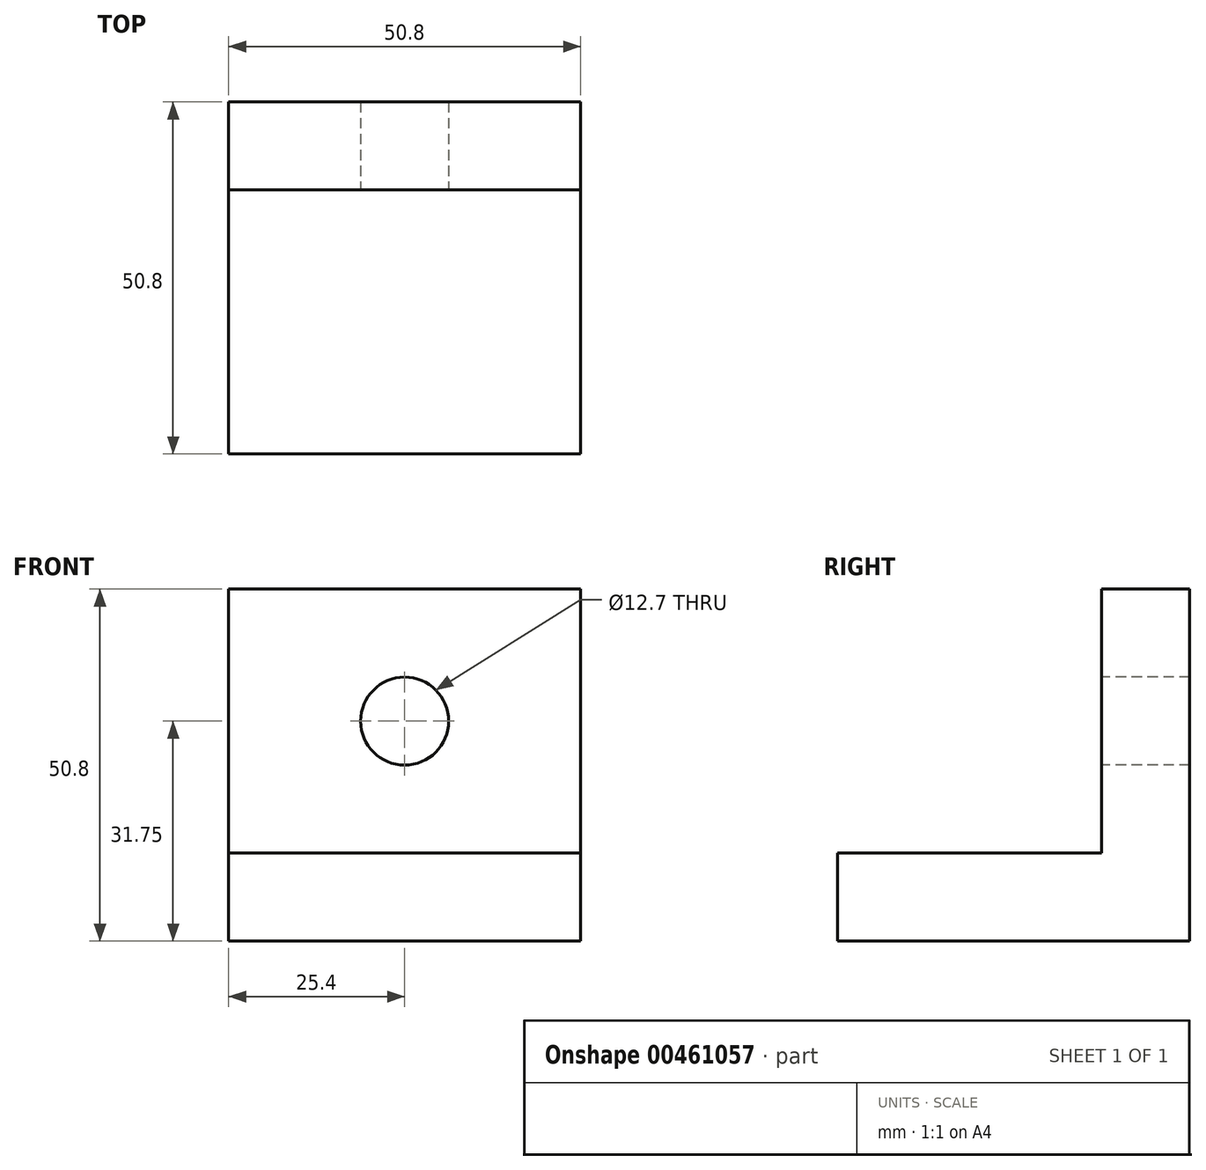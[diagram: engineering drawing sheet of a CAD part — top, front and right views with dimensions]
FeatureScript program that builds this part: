
annotation { "Feature Type Name" : "Feature", "Feature Type Description" : "" }
export const myFeature = defineFeature(function(context is Context, id is Id, definition is map)
    precondition{}
    {
        {
            var Q0;
            Q0=qCreatedBy(makeId("Right.planeOp"),FACE);
            var sketch = newSketch(context, id + "F0", { "sketchPlane" : qUnion([Q0])});
            skLineSegment(sketch, "E0", {"start": v(0, 0) * mm, "end": v(0, 50.8) * mm});
            skLineSegment(sketch, "E1", {"start": v(0, 0) * mm, "end": v(-50.8, 0) * mm});
            skLineSegment(sketch, "E2", {"start": v(-50.8, 0) * mm, "end": v(-50.8, 12.7) * mm});
            skLineSegment(sketch, "E3", {"start": v(0, 50.8) * mm, "end": v(-12.7, 50.8) * mm});
            skLineSegment(sketch, "E4", {"start": v(-50.8, 12.7) * mm, "end": v(-12.7, 12.7) * mm});
            skLineSegment(sketch, "E5", {"start": v(-12.7, 12.7) * mm, "end": v(-12.7, 50.8) * mm});
            skSolve(sketch);
        }
        {
            var Q0;
            Q0 = qSketchRegion(id + "F0", true);
            extrude(context, id + "F1", {"entities" : qUnion([Q0]), "depth" : 50.8 * mm});
        }
        {
            var Q0;
            Q0=makeQuery(id+"F1.opExtrude","SWEPT_FACE",FACE,{"disambiguationData":[OSD([sQuery(id+"F0.wireOp",EDGE,"E5")])]});
            var sketch = newSketch(context, id + "F2", { "sketchPlane" : qUnion([Q0])});
            skCircle(sketch, "E6", {"center": v(25.4, 31.75) * mm, "radius": 6.35 * mm});
            skPoint(sketch, "E6.centerSnap0", {"position": v(0, 31.75) * mm});
            skPoint(sketch, "E6.centerSnap1", {"position": v(25.4, 50.8) * mm});
            skSolve(sketch);
        }
        {
            var Q0;
            Q0 = qSketchRegion(id + "F2", true);
            extrude(context, id + "F3", {"entities" : qUnion([Q0]), "operationType" : NewBodyOperationType.REMOVE, "oppositeDirection" : true, "depth" : 25.4 * mm});
        }
    });
